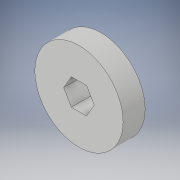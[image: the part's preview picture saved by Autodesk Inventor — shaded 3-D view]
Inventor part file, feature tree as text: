
AUTODESK INVENTOR PART (.ipt)
format: ipt  version: 2018 (Build 220112000, 112)  size: 102,912 bytes
history: native  units: in
note: dims shown in document units (in); Inventor stores cm internally (conversion verified against a paired STEP export)
features: extrude x1, sketch x1
ambient origin geometry x8: Origin, YZ Plane, XZ Plane, XY Plane, X Axis, Y Axis, Z Axis, Center Point
bodies: Solid1 (feature_tree)
feature tree (2):
  extrude  "Extrusion1"  Depth=0.3in
  sketch  "Sketch1"  dims[d0=1.0in d1=0.3in d2=0.25in d3=0.0in]
